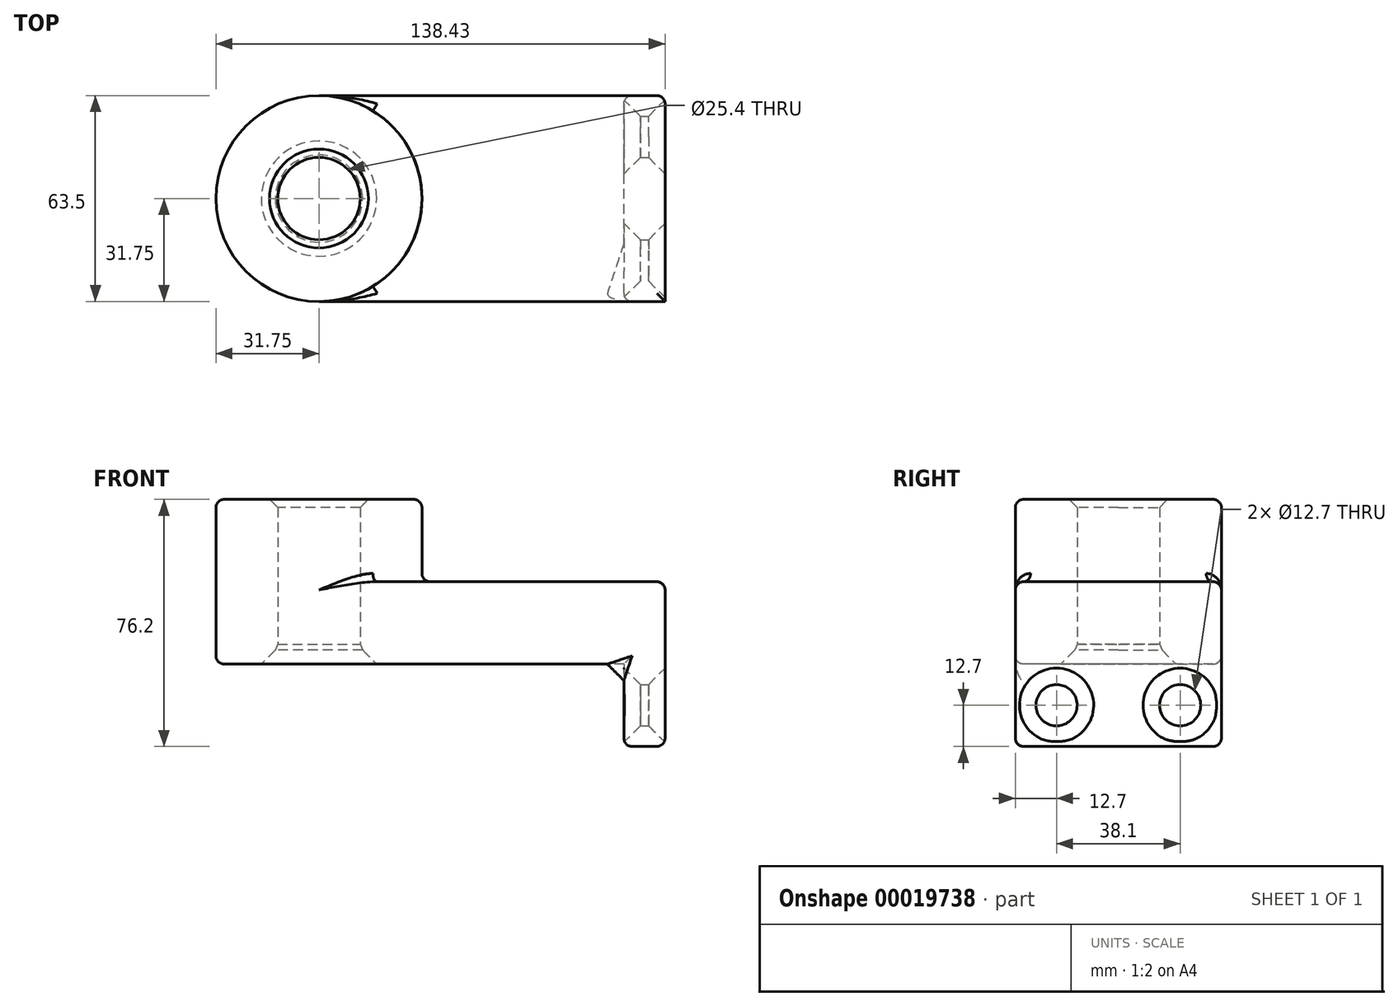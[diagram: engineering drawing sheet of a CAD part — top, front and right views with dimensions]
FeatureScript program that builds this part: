
annotation { "Feature Type Name" : "Feature", "Feature Type Description" : "" }
export const myFeature = defineFeature(function(context is Context, id is Id, definition is map)
    precondition{}
    {
        {
            var Q0;
            Q0=qCreatedBy(makeId("Top.planeOp"),FACE);
            var sketch = newSketch(context, id + "F0", { "sketchPlane" : qUnion([Q0])});
            skLineSegment(sketch, "E0.rect.bottom", {"start": v(53.34, -31.75) * mm, "end": v(-53.34, -31.75) * mm});
            skLineSegment(sketch, "E0.rect.top", {"start": v(53.34, 31.75) * mm, "end": v(-53.34, 31.75) * mm});
            skLineSegment(sketch, "E0.rect.left", {"start": v(53.34, -31.75) * mm, "end": v(53.34, 31.75) * mm});
            skLineSegment(sketch, "E0.rect.right", {"start": v(-53.34, -31.75) * mm, "end": v(-53.34, 31.75) * mm});
            skPoint(sketch, "E0.rect.middle", {"position": v(0, 0) * mm});
            skCircle(sketch, "E1", {"center": v(-53.34, 0) * mm, "radius": 31.75 * mm});
            skCircle(sketch, "E2", {"center": v(-53.34, 0) * mm, "radius": 12.7 * mm});
            skSolve(sketch);
        }
        {
            var Q0;
            Q0 = qSketchRegion(id + "F0", true);
            extrude(context, id + "F1", {"entities" : qUnion([Q0]), "depth" : 12.7 * mm});
        }
        {
            var Q0;
            {var subQ0=sQuery(id+"F0.wireOp",EDGE,"E2");var subQ1=sQuery(id+"F0.wireOp",EDGE,"E0.rect.right");var subQ3=makeQuery(id+"F0.imprint","INTERSECT",VERTEX,{"disambiguationData":[OD(0.0)],"derivedFrom":[subQ1,subQ0]});Q0=makeQuery(id+"F0.imprint","IMPRINT",FACE,{"disambiguationData":[TD([[makeQuery(id+"F0.imprint","IMPRINT",EDGE,{"disambiguationData":[TD([[subQ3,-1.0]])],"derivedFrom":subQ0}),-1.0]])]});}
            var Q1;
            {var subQ0=sQuery(id+"F0.wireOp",EDGE,"E2");var subQ1=sQuery(id+"F0.wireOp",EDGE,"E0.rect.right");var subQ3=makeQuery(id+"F0.imprint","INTERSECT",VERTEX,{"disambiguationData":[OD(0.0)],"derivedFrom":[subQ1,subQ0]});Q1=makeQuery(id+"F0.imprint","IMPRINT",FACE,{"disambiguationData":[TD([[makeQuery(id+"F0.imprint","IMPRINT",EDGE,{"disambiguationData":[TD([[subQ3,1.0]])],"derivedFrom":subQ0}),-1.0]])]});}
            extrude(context, id + "F2", {"entities" : qUnion([Q0, Q1]), "operationType" : NewBodyOperationType.ADD, "depth" : 50.8 * mm});
        }
        {
            var Q0;
            Q0=makeQuery(id+"F1.opExtrude","SWEPT_FACE",FACE,{"disambiguationData":[OSD([sQuery(id+"F0.wireOp",EDGE,"E0.rect.left")])]});
            var sketch = newSketch(context, id + "F3", { "sketchPlane" : qUnion([Q0])});
            skLineSegment(sketch, "E3.bottom", {"start": v(-31.75, 12.7) * mm, "end": v(31.75, 12.7) * mm});
            skLineSegment(sketch, "E3.top", {"start": v(-31.75, -25.4) * mm, "end": v(31.75, -25.4) * mm});
            skLineSegment(sketch, "E3.left", {"start": v(-31.75, 12.7) * mm, "end": v(-31.75, -25.4) * mm});
            skLineSegment(sketch, "E3.right", {"start": v(31.75, 12.7) * mm, "end": v(31.75, -25.4) * mm});
            skCircle(sketch, "E4", {"center": v(-19.05, -12.7) * mm, "radius": 6.35 * mm});
            skLineSegment(sketch, "E5", {"start": v(0, 0) * mm, "end": v(0, -25.4) * mm, "construction": true});
            skCircle(sketch, "E6.MirrorC", {"center": v(19.05, -12.7) * mm, "radius": 6.35 * mm});
            skSolve(sketch);
        }
        {
            var Q0;
            Q0 = qSketchRegion(id + "F0", true);
            extrude(context, id + "F4", {"entities" : qUnion([Q0]), "operationType" : NewBodyOperationType.ADD, "depth" : 25.4 * mm});
        }
        {
            var Q0;
            {var subQ2=sQuery(id+"F3.wireOp",EDGE,"E3.top");Q0=makeQuery(id+"F3.imprint","IMPRINT",FACE,{"disambiguationData":[TD([[makeQuery(id+"F3.imprint","IMPRINT",EDGE,{"derivedFrom":subQ2}),1.0]])]});}
            extrude(context, id + "F5", {"entities" : qUnion([Q0]), "operationType" : NewBodyOperationType.ADD, "oppositeDirection" : true, "depth" : 12.7 * mm});
        }
        {
            var Q0;
            {var subQ0=sQuery(id+"F0.wireOp",EDGE,"E1");Q0=makeQuery(id+"F4.boolean.opBoolean","INTERSECT",EDGE,{"derivedFrom":[makeQuery(id+"F2.boolean.opBoolean","MERGE",FACE,{"derivedFrom":[makeQuery(id+"F1.opExtrude","SWEPT_FACE",FACE,{"disambiguationData":[OSD([subQ0])]}),makeQuery(id+"F2.opExtrude","SWEPT_FACE",FACE,{"disambiguationData":[OSD([subQ0])]})]}),makeQuery(id+"F4.opExtrude","CAP_FACE",FACE,{"disambiguationData":[OSD([sQuery(id+"F0.wireOp",EDGE,"E0.rect.bottom"),sQuery(id+"F0.wireOp",EDGE,"E0.rect.top"),sQuery(id+"F0.wireOp",EDGE,"E0.rect.left"),subQ0,sQuery(id+"F0.wireOp",EDGE,"E2")])],"isStart":false})]});}
            var Q1;
            Q1=makeQuery(id+"F4.opExtrude","CAP_EDGE",EDGE,{"disambiguationData":[OSD([sQuery(id+"F0.wireOp",EDGE,"E0.rect.left")])],"isStart":false});
            var Q2;
            Q2=makeQuery(id+"F5.opExtrude","CAP_EDGE",EDGE,{"disambiguationData":[OSD([sQuery(id+"F3.wireOp",EDGE,"E3.top")])],"isStart":true});
            var Q3;
            Q3=makeQuery(id+"F4.opExtrude","CAP_EDGE",EDGE,{"disambiguationData":[OSD([sQuery(id+"F0.wireOp",EDGE,"E0.rect.bottom")])],"isStart":false});
            var Q4;
            Q4=makeQuery(id+"F4.opExtrude","CAP_EDGE",EDGE,{"disambiguationData":[OSD([sQuery(id+"F0.wireOp",EDGE,"E0.rect.top")])],"isStart":false});
            var Q5;
            {var subQ0=sQuery(id+"F0.wireOp",EDGE,"E0.rect.top");var subQ1=sQuery(id+"F0.wireOp",EDGE,"E0.rect.left");Q5=makeQuery(id+"F5.boolean.opBoolean","MERGE",EDGE,{"derivedFrom":[makeQuery(id+"F4.boolean.opBoolean","MERGE",EDGE,{"derivedFrom":[makeQuery(id+"F1.opExtrude","SWEPT_EDGE",EDGE,{"disambiguationData":[OSD([subQ0,subQ1])]}),makeQuery(id+"F4.opExtrude","SWEPT_EDGE",EDGE,{"disambiguationData":[OSD([subQ0,subQ1])]})]}),makeQuery(id+"F5.opExtrude","CAP_EDGE",EDGE,{"disambiguationData":[OSD([sQuery(id+"F3.wireOp",EDGE,"E3.right")])],"isStart":true})]});}
            var Q6;
            Q6=makeQuery(id+"F5.opExtrude","CAP_EDGE",EDGE,{"disambiguationData":[OSD([sQuery(id+"F3.wireOp",EDGE,"E3.right")])],"isStart":false});
            var Q7;
            Q7=makeQuery(id+"F5.opExtrude","CAP_EDGE",EDGE,{"disambiguationData":[OSD([sQuery(id+"F3.wireOp",EDGE,"E3.left")])],"isStart":false});
            var Q8;
            Q8=makeQuery(id+"F1.opExtrude","CAP_EDGE",EDGE,{"disambiguationData":[OSD([sQuery(id+"F0.wireOp",EDGE,"E0.rect.bottom")])],"isStart":true});
            var Q9;
            Q9=makeQuery(id+"F1.opExtrude","CAP_EDGE",EDGE,{"disambiguationData":[OSD([sQuery(id+"F0.wireOp",EDGE,"E1")])],"isStart":true});
            var Q10;
            Q10=makeQuery(id+"F2.opExtrude","CAP_EDGE",EDGE,{"disambiguationData":[OSD([sQuery(id+"F0.wireOp",EDGE,"E1")])],"isStart":false});
            var Q11;
            Q11=makeQuery(id+"F5.opExtrude","CAP_EDGE",EDGE,{"disambiguationData":[OSD([sQuery(id+"F3.wireOp",EDGE,"E3.top")])],"isStart":false});
            var Q12;
            Q12=makeQuery(id+"F5.opExtrude","SWEPT_EDGE",EDGE,{"disambiguationData":[OSD([sQuery(id+"F3.wireOp",EDGE,"E3.top"),sQuery(id+"F3.wireOp",EDGE,"E3.right")])]});
            var Q13;
            Q13=makeQuery(id+"F5.opExtrude","SWEPT_EDGE",EDGE,{"disambiguationData":[OSD([sQuery(id+"F3.wireOp",EDGE,"E3.top"),sQuery(id+"F3.wireOp",EDGE,"E3.left")])]});
            fillet(context, id + "F6", {"entities" : qUnion([Q0, Q1, Q2, Q3, Q4, Q5, Q6, Q7, Q8, Q9, Q10, Q11, Q12, Q13]), "radius" : 2.54 * mm, "tangentPropagation" : true, "allowEdgeOverflow" : false});
        }
        {
            var Q0;
            Q0=makeQuery(id+"F6.opFillet","BLEND_FACE",FACE,{"disambiguationData":[OSD([sQuery(id+"F3.wireOp",EDGE,"E3.left")])]});
            var Q1;
            {var subQ0=sQuery(id+"F3.wireOp",EDGE,"E3.left");var subQ1=sQuery(id+"F0.wireOp",EDGE,"E0.rect.bottom");Q1=makeQuery(id+"F6.opFillet","BLEND_EDGE",EDGE,{"blendedFrom":[makeQuery(id+"F5.opExtrude","CAP_EDGE",EDGE,{"disambiguationData":[OSD([subQ0])],"isStart":false}),makeQuery(id+"F5.boolean.opBoolean","MERGE",FACE,{"derivedFrom":[makeQuery(id+"F4.boolean.opBoolean","MERGE",FACE,{"derivedFrom":[makeQuery(id+"F1.opExtrude","SWEPT_FACE",FACE,{"disambiguationData":[OSD([subQ1])]}),makeQuery(id+"F4.opExtrude","SWEPT_FACE",FACE,{"disambiguationData":[OSD([subQ1])]})]}),makeQuery(id+"F5.opExtrude","SWEPT_FACE",FACE,{"disambiguationData":[OSD([subQ0])]})]})],"blendedInto":[makeQuery(id+"F5.boolean.opBoolean","MERGE",FACE,{"derivedFrom":[makeQuery(id+"F4.boolean.opBoolean","MERGE",FACE,{"derivedFrom":[makeQuery(id+"F1.opExtrude","SWEPT_FACE",FACE,{"disambiguationData":[OSD([subQ1])]}),makeQuery(id+"F4.opExtrude","SWEPT_FACE",FACE,{"disambiguationData":[OSD([subQ1])]})]}),makeQuery(id+"F5.opExtrude","SWEPT_FACE",FACE,{"disambiguationData":[OSD([subQ0])]})]})]});}
            var Q2;
            Q2=makeQuery(id+"F1.opExtrude","CAP_EDGE",EDGE,{"disambiguationData":[OSD([sQuery(id+"F0.wireOp",EDGE,"E2")])],"isStart":true});
            chamfer(context, id + "F7", {"entities" : qUnion([Q0, Q1, Q2]), "width" : 5.08 * mm, "tangentPropagation" : true});
        }
        {
            var Q0;
            {var subQ0=sQuery(id+"F0.wireOp",EDGE,"E2");Q0=makeQuery(id+"F2.boolean.opBoolean","MERGE",FACE,{"derivedFrom":[makeQuery(id+"F1.opExtrude","SWEPT_FACE",FACE,{"disambiguationData":[OSD([subQ0])]}),makeQuery(id+"F2.opExtrude","SWEPT_FACE",FACE,{"disambiguationData":[OSD([subQ0])]})]});}
            chamfer(context, id + "F8", {"entities" : qUnion([Q0]), "width" : 2.54 * mm, "tangentPropagation" : true});
        }
        {
            var Q0;
            Q0=makeQuery(id+"F2.opExtrude","CAP_EDGE",EDGE,{"disambiguationData":[OSD([sQuery(id+"F0.wireOp",EDGE,"E2")])],"isStart":false});
            var Q1;
            Q1=makeQuery(id+"F1.opExtrude","CAP_EDGE",EDGE,{"disambiguationData":[OSD([sQuery(id+"F0.wireOp",EDGE,"E2")])],"isStart":true});
            var Q2;
            Q2=makeQuery(id+"F5.opExtrude","CAP_EDGE",EDGE,{"disambiguationData":[OSD([sQuery(id+"F3.wireOp",EDGE,"E4")])],"isStart":false});
            var Q3;
            Q3=makeQuery(id+"F5.opExtrude","CAP_EDGE",EDGE,{"disambiguationData":[OSD([sQuery(id+"F3.wireOp",EDGE,"E6.MirrorC")])],"isStart":false});
            var Q4;
            Q4=makeQuery(id+"F5.opExtrude","CAP_EDGE",EDGE,{"disambiguationData":[OSD([sQuery(id+"F3.wireOp",EDGE,"E4")])],"isStart":true});
            var Q5;
            Q5=makeQuery(id+"F5.opExtrude","CAP_EDGE",EDGE,{"disambiguationData":[OSD([sQuery(id+"F3.wireOp",EDGE,"E6.MirrorC")])],"isStart":true});
            chamfer(context, id + "F9", {"entities" : qUnion([Q0, Q1, Q2, Q3, Q4, Q5]), "width" : 5.08 * mm, "tangentPropagation" : true});
        }
    });
